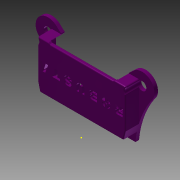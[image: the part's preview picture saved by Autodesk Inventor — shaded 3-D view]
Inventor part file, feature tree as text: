
AUTODESK INVENTOR PART (.ipt)
format: ipt  version: 2015 (Build 190159000, 159)  size: 711,168 bytes
history: native  units: mm
features: sketch x17, extrude x16, fillet x6, projected_geometry x5, plane x2
ambient origin geometry x8: Origin, YZ Plane, XZ Plane, XY Plane, X Axis, Y Axis, Z Axis, Center Point
bodies: Solid1 (feature_tree)
feature tree (46):
  extrude  "Extrusion1"  Depth=1.0mm
  extrude  "Extrusion2"  Depth=1.0mm
  extrude  "Extrusion3"  Depth=3.5mm TaperAngle=0.0deg
  extrude  "Extrusion4"  Depth=13.5mm TaperAngle=0.0deg
  extrude  "Extrusion5"  Depth=13.5mm TaperAngle=0.0deg
  extrude  "Extrusion6"  Depth=13.5mm TaperAngle=0.0deg
  extrude  "Extrusion7"  Depth=13.5mm TaperAngle=0.0deg
  extrude  "Extrusion8"  Depth=1.0mm TaperAngle=0.0deg
  plane  "Work Plane1"
  extrude  "Extrusion9"  Depth=1.0mm TaperAngle=0.0deg
  extrude  "Extrusion10"  Depth=3.5mm TaperAngle=0.0deg
  extrude  "Extrusion11"  Depth=3.5mm TaperAngle=0.0deg
  fillet  "Fillet1"  Radius=1.0mm
  fillet  "Fillet2"  Radius=1.0mm
  fillet  "Fillet3"  Radius=1.0mm
  fillet  "Fillet4"  Radius=1.0mm
  fillet  "Fillet5"  Radius=1.0mm
  fillet  "Fillet6"  Radius=1.0mm
  plane  "Work Plane2"
  extrude  "Extrusion12"  Depth=4.125mm
  extrude  "Extrusion13"  TaperAngle=45.0deg  [1 undecoded]
  sketch  "Sketch18"  dims[d47=50.0mm d48=0.0mm d49=3.178712mm d50=26.452487mm]
  extrude  "Extrusion16"  Depth=3.178712mm
  extrude  "Extrusion18"  TaperAngle=90.0deg  [1 undecoded]
  extrude  "Extrusion19"  Depth=1.0mm
  sketch  "Sketch23"  dims[d68=1.0mm d69=1.0mm d73=3.5mm d74=0.0mm d83=0.25mm d84=0.25mm d85=0.25mm d86=3.5mm d87=0.0mm d91=3.5mm d92=0.0mm]
  sketch  "Sketch1"  dims[d0=1.0mm d1=1.0mm]
  sketch  "Sketch3"  dims[d2=1.0mm d3=1.0mm]
  sketch  "Sketch4"  dims[d4=1.0mm d6=3.5mm d7=0.0mm]
  sketch  "Sketch5"  dims[d9=180.0deg d10=13.5mm d11=0.0mm]
  sketch  "Sketch6"  dims[d12=90.0deg d13=13.5mm d14=0.0mm]
  sketch  "Sketch7"  dims[d15=90.0deg d16=13.5mm d17=0.0mm]
  sketch  "Sketch8"  dims[d18=13.5mm d19=0.0mm d20=13.5mm d21=0.0mm]
  sketch  "Sketch9"  dims[d22=1.0mm d23=13.5mm d24=0.0mm]
  sketch  "Sketch10"  dims[d25=1.0mm d26=13.5mm d27=0.0mm]
  sketch  "Sketch11"  dims[d28=-13.5mm d29=3.5mm d30=0.0mm]
  projected_geometry  "Projected Loop1"
  sketch  "Sketch12"  dims[d31=3.5mm d32=0.0mm d33=3.5mm d34=0.0mm d35=1.0mm d38=1.0mm d39=1.0mm d40=1.0mm d41=1.0mm d42=1.0mm]
  projected_geometry  "Projected Loop2"
  sketch  "Sketch15"  dims[d43=0.0mm d44=4.125mm]
  sketch  "Sketch16"  dims[d45=90.0deg d46=45.0deg]
  projected_geometry  "Projected Loop4"
  projected_geometry  "Projected Loop5"
  projected_geometry  "Projected Loop6"
  sketch  "Sketch19"  dims[d51=50.0mm d52=0.0mm d61=90.0deg]
  sketch  "Sketch20"  dims[d64=1.0mm d65=1.0mm]
note: 2 required parameter values undecoded (feature->parameter linkage not recoverable at this tier; creation-order binding heuristic only, values carry confidence <= 0.55)
